# Revit family: Shower-Shower_Trim-KOHLER-Fairfax-K-TS12014_1
name_source: partatom
category: Plumbing Fixtures
revit_build: Autodesk Revit 2015 (Build: 20140606_1530(x64)
units: mm (PartAtom-declared; Revit-internal decimal feet)

## types (6) — shared parameters
ADA Compliant = No
Assembly Code = D2010700
CW Connection = No
Cold Water Inlet = Cold Water Inlet
Date Modified = 04/16/2019
Default Elevation = 42"
Drain Included = No
HW Connection = Yes
Handle Clearance = 3 7/16"
Height = 6 1/2"
Hot Water Inlet = Tempered Water Inlet
Length = 5 5/8"
Manufacturer = KOHLER Co.
MasterFormat 1995 = 15410
MasterFormat 2004 = 22.41.23
Material = Premium Metal Construction
Pressure = 80.00 psi
Product Documentation Link = https://www.us.kohler.com
Product Name = Fairfax
Product Page URL = http://www.us.kohler.com
URL = https://www.us.kohler.com
Vent Connection = No
Waste Connection = No
Waste Water Outlet = Waste Water Outlet
Width = 6 1/2"

## per-type parameters (varying)
| type | 2.0 gpm Showerhead | 2.5 gpm Showerhead | Description | Finish | Flow Rate | Model | Type | WaterSense Certified |
| 2.5 gpm Showerhead, CP-Polished Chrome | No | Yes | Rite-Temp shower valve trim with lever handle and 2.5 gpm showerhead | Kohler-Metal-CP-Polished_Chrome | 3 GPM | K-TS12014-4-CP | 1 | No |
| 2.5 gpm Showerhead, BN-Vibrant Brushed Nickel | No | Yes | Rite-Temp shower valve trim with lever handle and 2.5 gpm showerhead | Kohler-Metal-BN-Vibrant_Brushed_Nickel | 3 GPM | K-TS12014-4-BN | 2 | No |
| 2.5 gpm Showerhead, 2BZ-Oil-Rubbed Bronze | No | Yes | Rite-Temp shower valve trim with lever handle and 2.5 gpm showerhead | Kohler-Metal-2BZ-Oil_Rubbed_Bronze | 3 GPM | K-TS12014-4-2BZ | 3 | No |
| 2.0 gpm Showerhead, CP-Polished Chrome | Yes | No | Rite-Temp(r) shower trim set, valve not included | Kohler-Metal-CP-Polished_Chrome | 2 GPM | K-TS12014-4E-CP | 4 | Yes |
| 2.0 gpm Showerhead, BN-Vibrant Brushed Nickel | Yes | No | Rite-Temp(r) shower trim set, valve not included | Kohler-Metal-BN-Vibrant_Brushed_Nickel | 2 GPM | K-TS12014-4E-BN | 5 | Yes |
| 2.0 gpm Showerhead, 2BZ-Oil-Rubbed Bronze | Yes | No | Rite-Temp(r) shower trim set, valve not included | Kohler-Metal-2BZ-Oil_Rubbed_Bronze | 2 GPM | K-TS12014-4E-2BZ | 6 | Yes |

## geometry (parser evidence)
native form markers: Sweep x8
no freeform markers — native parametric forms only
